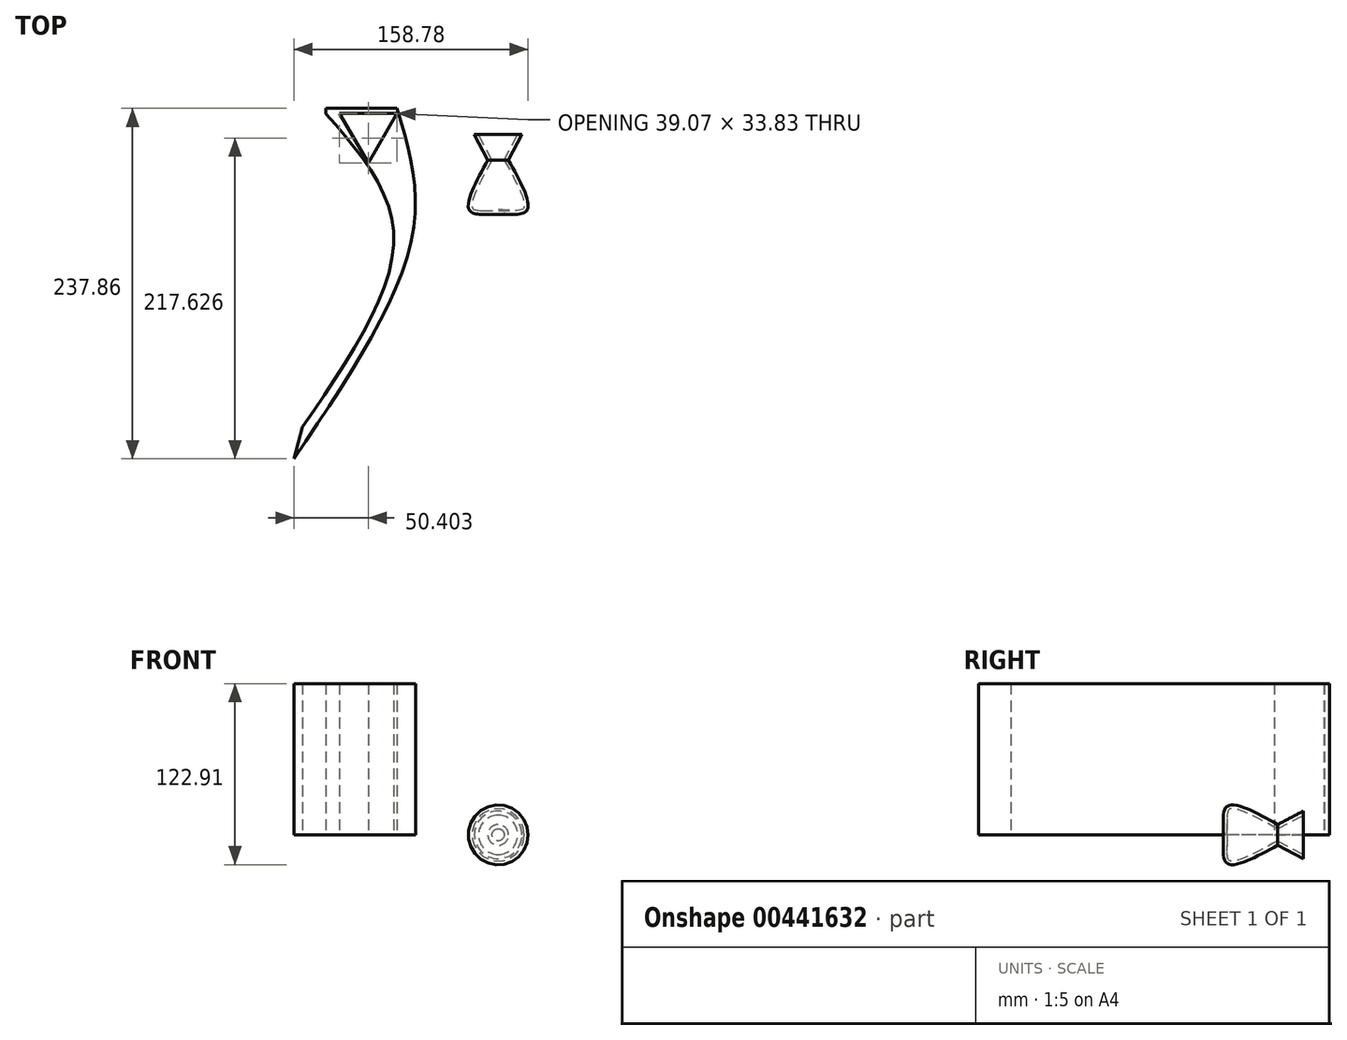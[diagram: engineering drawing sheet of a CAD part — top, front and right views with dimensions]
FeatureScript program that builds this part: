
annotation { "Feature Type Name" : "Feature", "Feature Type Description" : "" }
export const myFeature = defineFeature(function(context is Context, id is Id, definition is map)
    precondition{}
    {
        {
            var Q0;
            Q0=qCreatedBy(makeId("Top.planeOp"),FACE);
            var sketch = newSketch(context, id + "F0", { "sketchPlane" : qUnion([Q0])});
            skLineSegment(sketch, "E0", {"start": v(16.15, 23.32) * mm, "end": v(0, 23.32) * mm});
            skLineSegment(sketch, "E1", {"start": v(16.15, 23.32) * mm, "end": v(7.01, 5.94) * mm});
            skFitSpline(sketch, "E2", {"points": [v(7.01, 5.94) * mm, v(19.5, -28.2) * mm, v(0, -30.02) * mm], "startDerivative": vector(41.2, -75.02) * mm, "endDerivative": vector(-60.42, 7.3) * mm});
            skLineSegment(sketch, "E3", {"start": v(0, 45.87) * mm, "end": v(0, -46.18) * mm});
            skSolve(sketch);
        }
        {
            var Q0;
            {var subQ0=sQuery(id+"F0.wireOp",EDGE,"E0");Q0=makeQuery(id+"F0.imprint","IMPRINT",FACE,{"disambiguationData":[TD([[makeQuery(id+"F0.imprint","IMPRINT",EDGE,{"derivedFrom":subQ0}),1.0]])]});}
            var Q1;
            Q1=sQuery(id+"F0.wireOp",EDGE,"E3");
            revolve(context, id + "F1", {"entities" : qUnion([Q0]), "axis" : qUnion([Q1]), "revolveType" : RevolveType.FULL});
        }
        {
            var Q0;
            Q0=makeQuery(id+"F1.opRevolve","SWEPT_FACE",FACE,{"disambiguationData":[OSD([sQuery(id+"F0.wireOp",EDGE,"E0")])]});
            shell(context, id + "F2", {"entities" : qUnion([Q0]), "thickness" : 2.54 * mm});
        }
        {
            var Q0;
            Q0=qCreatedBy(makeId("Top.planeOp"),FACE);
            var sketch = newSketch(context, id + "F3", { "sketchPlane" : qUnion([Q0])});
            skLineSegment(sketch, "E4.0", {"start": v(-107.62, 37.64) * mm, "end": v(-68.55, 37.64) * mm});
            skLineSegment(sketch, "E4.2", {"start": v(-88.09, 3.81) * mm, "end": v(-107.62, 37.64) * mm});
            skPoint(sketch, "E4.0.midPoint", {"position": v(-88.09, 37.64) * mm});
            skPoint(sketch, "E4.cCircle.center.orphan", {"position": v(-88.09, 26.37) * mm});
            skFitSpline(sketch, "E5", {"points": [v(-116.9, 37.34) * mm, v(-70.88, -45.26) * mm, v(-132.67, -175.2) * mm], "startDerivative": vector(150.86, -173.12) * mm, "endDerivative": vector(-171.17, -249.3) * mm});
            skLineSegment(sketch, "E6", {"start": v(-68.55, 37.64) * mm, "end": v(-88.09, 3.81) * mm});
            skLineSegment(sketch, "E7", {"start": v(-116.9, 37.34) * mm, "end": v(-116.9, 40.96) * mm});
            skLineSegment(sketch, "E8", {"start": v(-116.9, 40.96) * mm, "end": v(-68.55, 40.96) * mm});
            skFitSpline(sketch, "E9", {"points": [v(-68.55, 40.96) * mm, v(-58.14, -45.26) * mm, v(-138.49, -196.9) * mm], "startDerivative": vector(58.85, -196.6) * mm, "endDerivative": vector(-185.02, -274.72) * mm});
            skFitSpline(sketch, "E10", {"points": [v(-138.49, -196.9) * mm, v(-132.67, -175.2) * mm], "startDerivative": vector(5.82, 21.7) * mm, "endDerivative": vector(5.82, 21.7) * mm});
            skSolve(sketch);
        }
        {
            var Q0;
            Q0=makeQuery(id+"F3.imprint","IMPRINT",FACE,{"disambiguationData":[TD([[makeQuery(id+"F3.imprint","IMPRINT",EDGE,{"derivedFrom":sQuery(id+"F3.wireOp",EDGE,"E4.0")}),1.0]])]});
            extrude(context, id + "F4", {"entities" : qUnion([Q0]), "depth" : 102.62 * mm});
        }
    });
